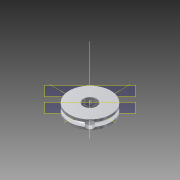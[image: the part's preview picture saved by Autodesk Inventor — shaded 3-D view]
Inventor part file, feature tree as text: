
AUTODESK INVENTOR PART (.ipt)
format: ipt  version: 2015 (Build 190159000, 159)  size: 212,992 bytes
history: native  units: mm
features: hole x4, sketch x3, plane x2, other x2, revolve x1, mirror x1
ambient origin geometry x8: Origin, YZ Plane, XZ Plane, XY Plane, X Axis, Y Axis, Z Axis, Center Point
bodies: Solid1 (feature_tree)
feature tree (13):
  revolve  "Revolution1"  [1 undecoded]
  hole  "Hole1"  [1 undecoded]
  hole  "Hole2"  [1 undecoded]
  plane  "Work Plane1"
  hole  "Hole3"  [1 undecoded]
  plane  "Work Plane2"
  other  "Work Point1"
  hole  "Hole4"  [1 undecoded]
  mirror  "Mirror2"
  sketch  "Sketch1"  dims[d0=12.5mm d3=1.5mm]
  sketch  "Sketch2"  dims[d4=360.0deg]
  sketch  "Sketch5"  dims[d17=10.0mm d18=10.0mm d7=8.0mm d8=6.0mm d9=4.0mm d10=2.0mm d11=90.0deg d12=8.0mm d13=20.594885mm d14=5.067344mm d15=1.25mm d16=2.0mm d19=2.459mm d20=6.0mm d21=6.3mm d22=2.0mm d23=90.0deg d24=8.8mm d25=20.594885mm d31=45.0deg d32=2.459mm d33=6.0mm d34=4.0mm d35=2.0mm d36=90.0deg d37=8.8mm d38=20.594885mm d39=10.0mm d40=10.0mm d41=5.0mm d42=6.0mm d43=4.0mm d44=2.0mm d45=90.0deg d46=3.0mm d47=20.594885mm]
  other  "Work Axis1"
note: 5 required parameter values undecoded (feature->parameter linkage not recoverable at this tier; creation-order binding heuristic only, values carry confidence <= 0.55)